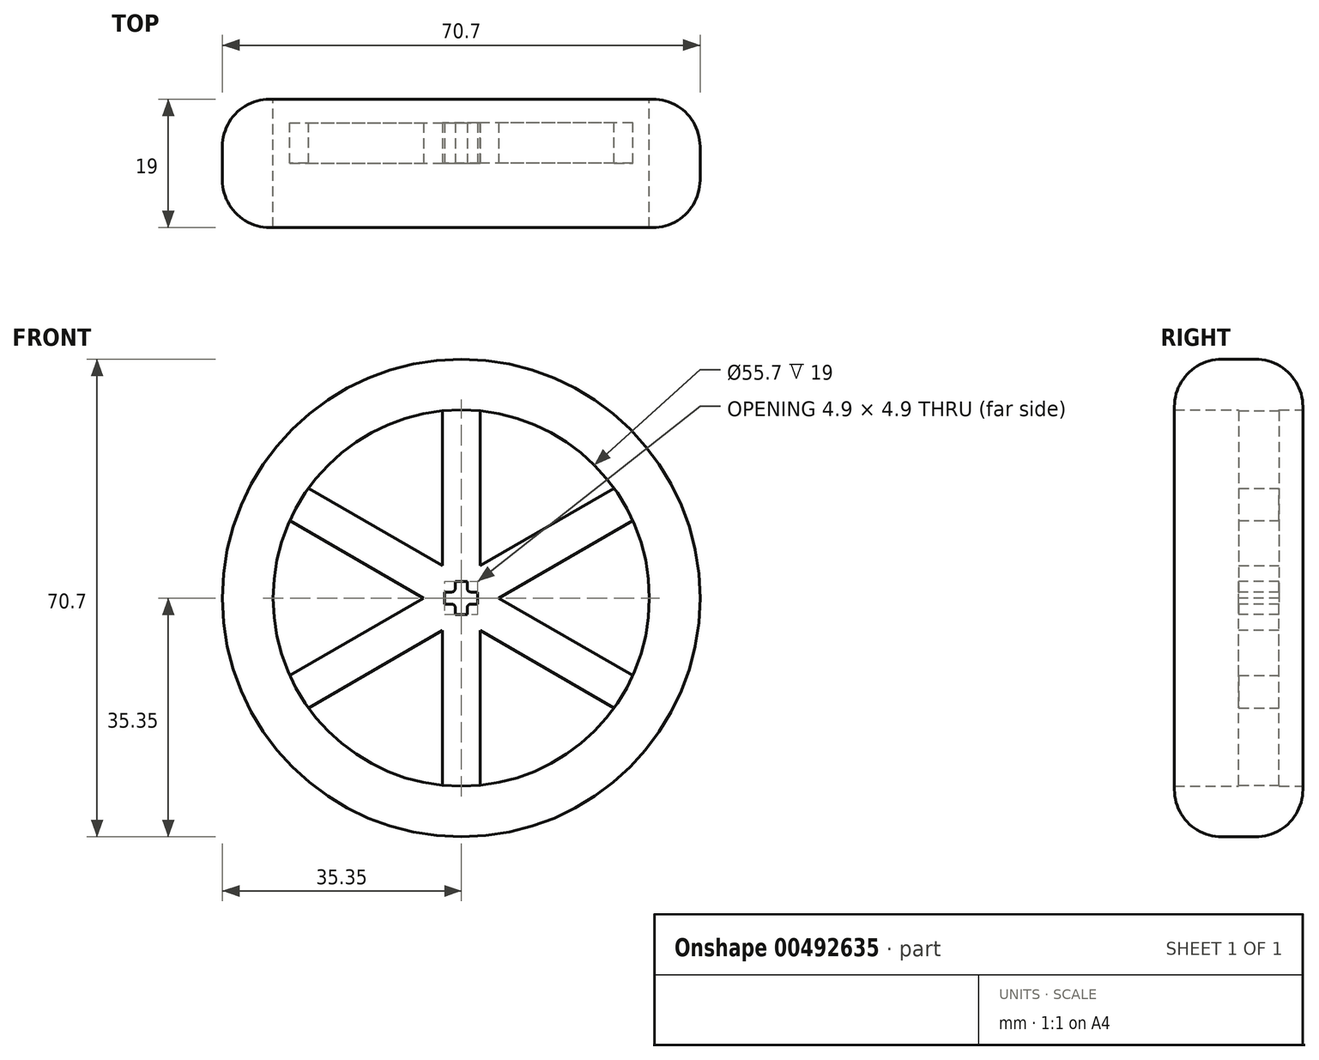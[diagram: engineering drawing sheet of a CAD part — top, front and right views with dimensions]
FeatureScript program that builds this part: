
annotation { "Feature Type Name" : "Feature", "Feature Type Description" : "" }
export const myFeature = defineFeature(function(context is Context, id is Id, definition is map)
    precondition{}
    {
        {
            var Q0;
            Q0=qCreatedBy(makeId("Front.planeOp"),FACE);
            var sketch = newSketch(context, id + "F0", { "sketchPlane" : qUnion([Q0])});
            skCircle(sketch, "E0", {"center": v(0, 0) * mm, "radius": 3.5 * mm});
            skCircle(sketch, "E1", {"center": v(0, 0) * mm, "radius": 27.85 * mm});
            skLineSegment(sketch, "E2", {"start": v(0, 27.85) * mm, "end": v(-2.78, 27.85) * mm});
            skLineSegment(sketch, "E3", {"start": v(0, 27.85) * mm, "end": v(2.77, 27.85) * mm});
            skLineSegment(sketch, "E4", {"start": v(2.77, 27.85) * mm, "end": v(2.77, 2.13) * mm});
            skLineSegment(sketch, "E5", {"start": v(-2.78, 27.85) * mm, "end": v(-2.78, 2.13) * mm});
            skCircle(sketch, "E6", {"center": v(0, 0) * mm, "radius": 35.35 * mm});
            skSolve(sketch);
        }
        {
            var Q0;
            {var subQ0=sQuery(id+"F0.wireOp",EDGE,"E4");var subQ1=sQuery(id+"F0.wireOp",EDGE,"E0");var subQ2=makeQuery(id+"F0.imprint","INTERSECT",VERTEX,{"derivedFrom":[subQ1,subQ0]});Q0=makeQuery(id+"F0.imprint","IMPRINT",FACE,{"disambiguationData":[TD([[makeQuery(id+"F0.imprint","IMPRINT",EDGE,{"disambiguationData":[TD([[subQ2,-1.0]])],"derivedFrom":subQ1}),-1.0]])]});}
            extrude(context, id + "F1", {"entities" : qUnion([Q0]), "endBound" : BoundingType.SYMMETRIC, "depth" : 6 * mm, "offsetDistance" : 25 * mm});
        }
        {
            var Q0;
            Q0=makeQuery(id+"F1.opExtrude","SWEPT_BODY",BODY,{"disambiguationData":[OSD([sQuery(id+"F0.wireOp",EDGE,"E0"),sQuery(id+"F0.wireOp",EDGE,"E1"),sQuery(id+"F0.wireOp",EDGE,"E4"),sQuery(id+"F0.wireOp",EDGE,"E5")])]});
            var Q1;
            Q1=sQuery(id+"F0.wireOp",EDGE,"E0");
            circularPattern(context, id + "F2", {"operationType" : NewBodyOperationType.ADD, "entities" : qUnion([Q0]), "axis" : qUnion([Q1]), "angle" : 360 * degree, "instanceCount" : 6, "equalSpace" : true});
        }
        {
            var Q0;
            {var subQ0=makeQuery(id+"F1.opExtrude","CAP_FACE",FACE,{"disambiguationData":[OSD([sQuery(id+"F0.wireOp",EDGE,"E0"),sQuery(id+"F0.wireOp",EDGE,"E1"),sQuery(id+"F0.wireOp",EDGE,"E4"),sQuery(id+"F0.wireOp",EDGE,"E5")])],"isStart":false});Q0=makeQuery(id+"F2.boolean.opBoolean","MERGE",FACE,{"derivedFrom":[subQ0,makeQuery(id+"F2.opPattern","COPY",FACE,{"derivedFrom":subQ0,"instanceName":"1"}),makeQuery(id+"F2.opPattern","COPY",FACE,{"derivedFrom":subQ0,"instanceName":"2"}),makeQuery(id+"F2.opPattern","COPY",FACE,{"derivedFrom":subQ0,"instanceName":"3"}),makeQuery(id+"F2.opPattern","COPY",FACE,{"derivedFrom":subQ0,"instanceName":"4"}),makeQuery(id+"F2.opPattern","COPY",FACE,{"derivedFrom":subQ0,"instanceName":"5"})]});}
            var sketch = newSketch(context, id + "F3", { "sketchPlane" : qUnion([Q0])});
            skCircle(sketch, "E7", {"center": v(0, 0) * mm, "radius": 27.85 * mm});
            skCircle(sketch, "E8", {"center": v(0, 0) * mm, "radius": 35.35 * mm});
            skSolve(sketch);
        }
        {
            var Q0;
            Q0=makeQuery(id+"F3.imprint","IMPRINT",FACE,{"disambiguationData":[TD([[makeQuery(id+"F3.imprint","IMPRINT",EDGE,{"derivedFrom":sQuery(id+"F3.wireOp",EDGE,"E8")}),1.0]])]});
            extrude(context, id + "F4", {"entities" : qUnion([Q0]), "operationType" : NewBodyOperationType.ADD, "endBound" : BoundingType.SYMMETRIC, "depth" : 19 * mm, "offsetDistance" : 25 * mm});
        }
        {
            var Q0;
            Q0=makeQuery(id+"F4.opExtrude","CAP_EDGE",EDGE,{"disambiguationData":[OSD([sQuery(id+"F3.wireOp",EDGE,"E8")])],"isStart":true});
            var Q1;
            Q1=makeQuery(id+"F4.opExtrude","CAP_EDGE",EDGE,{"disambiguationData":[OSD([sQuery(id+"F3.wireOp",EDGE,"E8")])],"isStart":false});
            fillet(context, id + "F5", {"entities" : qUnion([Q0, Q1]), "radius" : 7 * mm, "tangentPropagation" : true, "allowEdgeOverflow" : false});
        }
        {
            var Q0;
            Q0=qCreatedBy(makeId("Front.planeOp"),FACE);
            var sketch = newSketch(context, id + "F6", { "sketchPlane" : qUnion([Q0])});
            skCircle(sketch, "E9", {"center": v(0, 0) * mm, "radius": 3.5 * mm});
            skSolve(sketch);
        }
        {
            var Q0;
            Q0 = qSketchRegion(id + "F6", true);
            extrude(context, id + "F7", {"entities" : qUnion([Q0]), "operationType" : NewBodyOperationType.ADD, "endBound" : BoundingType.SYMMETRIC, "depth" : 6 * mm, "offsetDistance" : 25 * mm});
        }
        {
            var Q0;
            {var subQ0=makeQuery(id+"F1.opExtrude","CAP_FACE",FACE,{"disambiguationData":[OSD([sQuery(id+"F0.wireOp",EDGE,"E0"),sQuery(id+"F0.wireOp",EDGE,"E1"),sQuery(id+"F0.wireOp",EDGE,"E4"),sQuery(id+"F0.wireOp",EDGE,"E5")])],"isStart":false});Q0=makeQuery(id+"F7.boolean.opBoolean","MERGE",FACE,{"derivedFrom":[makeQuery(id+"F2.boolean.opBoolean","MERGE",FACE,{"derivedFrom":[subQ0,makeQuery(id+"F2.opPattern","COPY",FACE,{"derivedFrom":subQ0,"instanceName":"1"}),makeQuery(id+"F2.opPattern","COPY",FACE,{"derivedFrom":subQ0,"instanceName":"2"}),makeQuery(id+"F2.opPattern","COPY",FACE,{"derivedFrom":subQ0,"instanceName":"3"}),makeQuery(id+"F2.opPattern","COPY",FACE,{"derivedFrom":subQ0,"instanceName":"4"}),makeQuery(id+"F2.opPattern","COPY",FACE,{"derivedFrom":subQ0,"instanceName":"5"})]}),makeQuery(id+"F7.opExtrude","CAP_FACE",FACE,{"disambiguationData":[OSD([sQuery(id+"F6.wireOp",EDGE,"E9")])],"isStart":false})]});}
            var sketch = newSketch(context, id + "F8", { "sketchPlane" : qUnion([Q0])});
            skLineSegment(sketch, "E10", {"start": v(-2.45, 0.9) * mm, "end": v(2.45, 0.9) * mm});
            skLineSegment(sketch, "E11", {"start": v(2.45, -0.9) * mm, "end": v(-2.45, -0.9) * mm});
            skLineSegment(sketch, "E12", {"start": v(0.9, 2.45) * mm, "end": v(0.9, -2.45) * mm});
            skLineSegment(sketch, "E13", {"start": v(-0.9, -2.45) * mm, "end": v(-0.9, 2.45) * mm});
            skLineSegment(sketch, "E14", {"start": v(-0.9, 2.45) * mm, "end": v(0.9, 2.45) * mm});
            skLineSegment(sketch, "E15", {"start": v(-0.9, -2.45) * mm, "end": v(0.9, -2.45) * mm});
            skLineSegment(sketch, "E16", {"start": v(2.45, -0.9) * mm, "end": v(2.45, 0.9) * mm});
            skLineSegment(sketch, "E17", {"start": v(-2.45, 0.9) * mm, "end": v(-2.45, -0.9) * mm});
            skSolve(sketch);
        }
        {
            var Q0;
            Q0 = qSketchRegion(id + "F8", true);
            extrude(context, id + "F9", {"entities" : qUnion([Q0]), "operationType" : NewBodyOperationType.REMOVE, "oppositeDirection" : true, "depth" : 25 * mm, "offsetDistance" : 25 * mm});
        }
        {
            var Q0;
            Q0=makeQuery(id+"F9.boolean.opBoolean","COPY",EDGE,{"derivedFrom":makeQuery(id+"F9.opExtrude","SWEPT_EDGE",EDGE,{"disambiguationData":[OSD([sQuery(id+"F8.wireOp",EDGE,"E10"),sQuery(id+"F8.wireOp",EDGE,"E12")])]})});
            var Q1;
            Q1=makeQuery(id+"F9.boolean.opBoolean","COPY",EDGE,{"derivedFrom":makeQuery(id+"F9.opExtrude","SWEPT_EDGE",EDGE,{"disambiguationData":[OSD([sQuery(id+"F8.wireOp",EDGE,"E11"),sQuery(id+"F8.wireOp",EDGE,"E12")])]})});
            var Q2;
            Q2=makeQuery(id+"F9.boolean.opBoolean","COPY",EDGE,{"derivedFrom":makeQuery(id+"F9.opExtrude","SWEPT_EDGE",EDGE,{"disambiguationData":[OSD([sQuery(id+"F8.wireOp",EDGE,"E11"),sQuery(id+"F8.wireOp",EDGE,"E13")])]})});
            var Q3;
            Q3=makeQuery(id+"F9.boolean.opBoolean","COPY",EDGE,{"derivedFrom":makeQuery(id+"F9.opExtrude","SWEPT_EDGE",EDGE,{"disambiguationData":[OSD([sQuery(id+"F8.wireOp",EDGE,"E10"),sQuery(id+"F8.wireOp",EDGE,"E13")])]})});
            fillet(context, id + "F10", {"entities" : qUnion([Q0, Q1, Q2, Q3]), "radius" : 0.5 * mm, "tangentPropagation" : true, "allowEdgeOverflow" : false});
        }
    });
